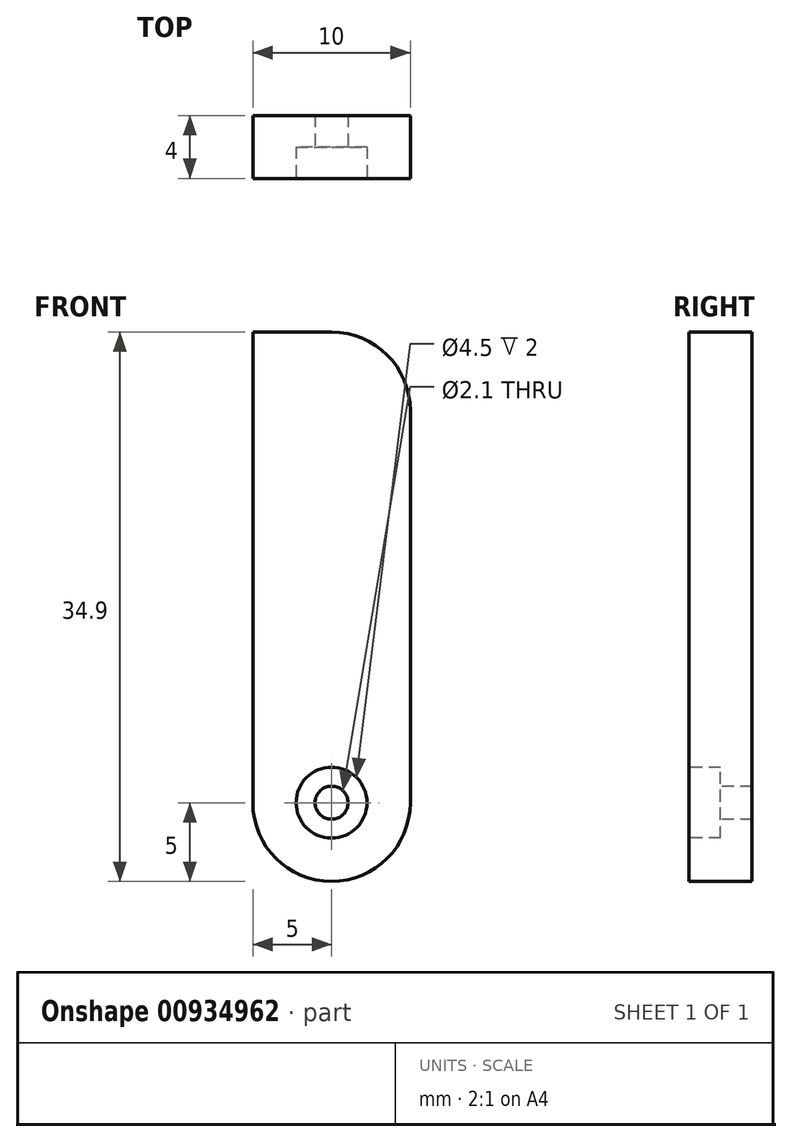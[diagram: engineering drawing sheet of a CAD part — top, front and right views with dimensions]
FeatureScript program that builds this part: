
annotation { "Feature Type Name" : "Feature", "Feature Type Description" : "" }
export const myFeature = defineFeature(function(context is Context, id is Id, definition is map)
    precondition{}
    {
        {
            var Q0;
            Q0=qCreatedBy(makeId("Front.planeOp"),FACE);
            var sketch = newSketch(context, id + "F0", { "sketchPlane" : qUnion([Q0])});
            skLineSegment(sketch, "E0.bottom", {"start": v(-5, -17.45) * mm, "end": v(5, -17.45) * mm});
            skLineSegment(sketch, "E0.top", {"start": v(-5, 17.45) * mm, "end": v(5, 17.45) * mm});
            skLineSegment(sketch, "E0.left", {"start": v(-5, -17.45) * mm, "end": v(-5, 17.45) * mm});
            skLineSegment(sketch, "E0.right", {"start": v(5, -17.45) * mm, "end": v(5, 17.45) * mm});
            skPoint(sketch, "E0.middle", {"position": v(0, 0) * mm});
            skSolve(sketch);
        }
        {
            var Q0;
            Q0 = qSketchRegion(id + "F0", true);
            extrude(context, id + "F1", {"entities" : qUnion([Q0]), "depth" : 4 * mm, "offsetDistance" : 25 * mm});
        }
        {
            var Q0;
            Q0=makeQuery(id+"F1.opExtrude","SWEPT_EDGE",EDGE,{"disambiguationData":[OSD([sQuery(id+"F0.wireOp",EDGE,"E0.top"),sQuery(id+"F0.wireOp",EDGE,"E0.right")])]});
            fillet(context, id + "F2", {"entities" : qUnion([Q0]), "radius" : 5 * mm, "tangentPropagation" : true, "allowEdgeOverflow" : false});
        }
        {
            var Q0;
            Q0=makeQuery(id+"F1.opExtrude","SWEPT_EDGE",EDGE,{"disambiguationData":[OSD([sQuery(id+"F0.wireOp",EDGE,"E0.bottom"),sQuery(id+"F0.wireOp",EDGE,"E0.right")])]});
            var Q1;
            Q1=makeQuery(id+"F1.opExtrude","SWEPT_EDGE",EDGE,{"disambiguationData":[OSD([sQuery(id+"F0.wireOp",EDGE,"E0.bottom"),sQuery(id+"F0.wireOp",EDGE,"E0.left")])]});
            fillet(context, id + "F3", {"entities" : qUnion([Q0, Q1]), "radius" : 5 * mm, "tangentPropagation" : true, "allowEdgeOverflow" : false});
        }
        {
            var Q0;
            Q0=makeQuery(id+"F1.opExtrude","CAP_FACE",FACE,{"disambiguationData":[OSD([sQuery(id+"F0.wireOp",EDGE,"E0.bottom"),sQuery(id+"F0.wireOp",EDGE,"E0.top"),sQuery(id+"F0.wireOp",EDGE,"E0.left"),sQuery(id+"F0.wireOp",EDGE,"E0.right")])],"isStart":false});
            var sketch = newSketch(context, id + "F4", { "sketchPlane" : qUnion([Q0])});
            skCircle(sketch, "E1", {"center": v(0, -12.45) * mm, "radius": 2.25 * mm});
            skCircle(sketch, "E2", {"center": v(0, -12.45) * mm, "radius": 1.05 * mm});
            skSolve(sketch);
        }
        {
            var Q0;
            Q0=makeQuery(id+"F4.imprint","IMPRINT",FACE,{"disambiguationData":[TD([[makeQuery(id+"F4.imprint","IMPRINT",EDGE,{"derivedFrom":sQuery(id+"F4.wireOp",EDGE,"E1")}),1.0]])]});
            extrude(context, id + "F5", {"entities" : qUnion([Q0]), "operationType" : NewBodyOperationType.REMOVE, "oppositeDirection" : true, "depth" : 2 * mm, "offsetDistance" : 25 * mm});
        }
        {
            var Q0;
            Q0=makeQuery(id+"F5.boolean.opBoolean","SPLIT",FACE,{"disambiguationData":[TD([makeQuery(id+"F5.opExtrude","SWEPT_FACE",FACE,{"disambiguationData":[OSD([sQuery(id+"F4.wireOp",EDGE,"E2")])]})])],"derivedFrom":makeQuery(id+"F1.opExtrude","CAP_FACE",FACE,{"disambiguationData":[OSD([sQuery(id+"F0.wireOp",EDGE,"E0.bottom"),sQuery(id+"F0.wireOp",EDGE,"E0.top"),sQuery(id+"F0.wireOp",EDGE,"E0.left"),sQuery(id+"F0.wireOp",EDGE,"E0.right")])],"isStart":false})});
            extrude(context, id + "F6", {"entities" : qUnion([Q0]), "operationType" : NewBodyOperationType.REMOVE, "oppositeDirection" : true, "depth" : 5 * mm, "offsetDistance" : 25 * mm});
        }
    });
